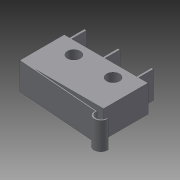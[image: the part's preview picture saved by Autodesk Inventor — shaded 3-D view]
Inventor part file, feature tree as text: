
AUTODESK INVENTOR PART (.ipt)
format: ipt  version: 2015 SP1 (Build 190203100, 203)  size: 119,296 bytes
history: native  units: mm
features: extrude x2, sketch x2
ambient origin geometry x8: Origin, YZ Plane, XZ Plane, XY Plane, X Axis, Y Axis, Z Axis, Center Point
bodies: Solid1 (feature_tree)
feature tree (4):
  extrude  "Extrusion1"  Depth=10.5mm
  extrude  "Extrusion2"  Depth=0.5mm
  sketch  "Sketch1"  dims[d0=19.75mm d1=10.5mm]
  sketch  "Sketch2"  dims[d2=14.0mm d3=0.5mm d4=6.35mm d5=0.0mm d6=3.0mm d7=3.0mm d8=5.25mm d9=5.25mm d10=0.3mm d11=13.75mm d12=0.785398mm d13=2.5mm d14=1.0mm d15=6.35mm d16=0.0mm d17=9.25mm]
